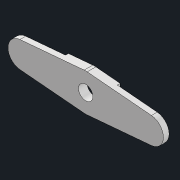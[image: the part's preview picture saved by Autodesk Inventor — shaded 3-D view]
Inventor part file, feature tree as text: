
AUTODESK INVENTOR PART (.ipt)
format: ipt  version: 2022.2 (Build 262287010, 287A)  size: 135,168 bytes
history: native  units: mm
features: extrude x2, sketch x2, projected_geometry x1
ambient origin geometry x8: Origin, YZ Plane, XZ Plane, XY Plane, X Axis, Y Axis, Z Axis, Center Point
bodies: Solid1 (feature_tree)
feature tree (5):
  extrude  "Extrusion1"  Depth=13.0mm
  extrude  "Extrusion2"  Depth=6.0mm
  sketch  "Sketch1"  dims[d0=54.0mm d1=13.0mm]
  sketch  "Sketch2"  dims[d2=5.0mm d4=6.0mm d5=2.0mm d6=0.0mm d7=18.0mm d8=9.0mm d9=1.0mm d10=0.0mm d11=1.745329mm]
  projected_geometry  "Projected Loop1"
